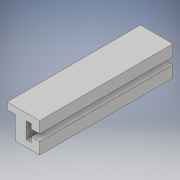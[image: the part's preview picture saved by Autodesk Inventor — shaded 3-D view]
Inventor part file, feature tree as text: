
AUTODESK INVENTOR PART (.ipt)
format: ipt  version: 2019 (Build 230136000, 136)  size: 111,104 bytes
history: native  units: mm
features: extrude x1, sketch x1
ambient origin geometry x8: Origin, YZ Plane, XZ Plane, XY Plane, X Axis, Y Axis, Z Axis, Center Point
bodies: Solid1 (feature_tree)
feature tree (2):
  extrude  "Extrusion1"  Depth=5.0mm
  sketch  "Sketch1"  dims[d0=6.0mm d1=5.0mm d2=6.3mm d3=6.3mm d4=3.8mm d6=8.375mm d8=5.0mm d10=5.0mm d12=3.5mm d13=3.8mm d14=17.3mm d15=100.0mm d16=0.0mm]
